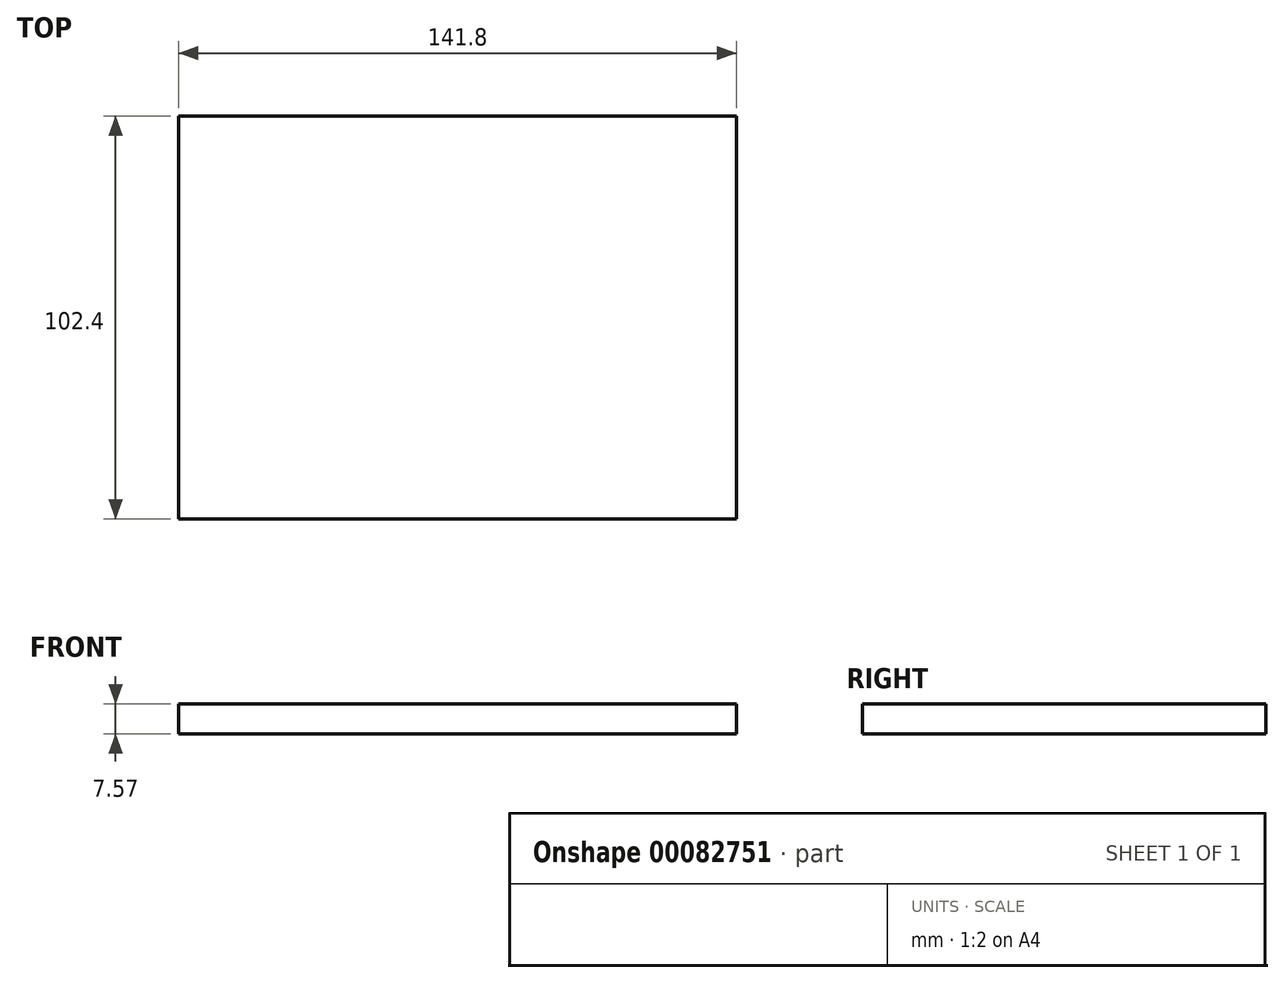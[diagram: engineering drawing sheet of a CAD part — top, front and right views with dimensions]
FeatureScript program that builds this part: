
annotation { "Feature Type Name" : "Feature", "Feature Type Description" : "" }
export const myFeature = defineFeature(function(context is Context, id is Id, definition is map)
    precondition{}
    {
        {
            var Q0;
            Q0=qCreatedBy(makeId("Top.planeOp"),FACE);
            var sketch = newSketch(context, id + "F0", { "sketchPlane" : qUnion([Q0])});
            skLineSegment(sketch, "E0.bottom", {"start": v(-70.05, 51.74) * mm, "end": v(71.75, 51.74) * mm});
            skLineSegment(sketch, "E0.top", {"start": v(-70.05, -50.66) * mm, "end": v(71.75, -50.66) * mm});
            skLineSegment(sketch, "E0.left", {"start": v(-70.05, 51.74) * mm, "end": v(-70.05, -50.66) * mm});
            skLineSegment(sketch, "E0.right", {"start": v(71.75, 51.74) * mm, "end": v(71.75, -50.66) * mm});
            skSolve(sketch);
        }
        {
            var Q0;
            Q0=makeQuery(id+"F0.imprint","IMPRINT",FACE,{"disambiguationData":[TD([[makeQuery(id+"F0.imprint","IMPRINT",EDGE,{"derivedFrom":sQuery(id+"F0.wireOp",EDGE,"E0.bottom")}),-1.0]])]});
            extrude(context, id + "F1", {"entities" : qUnion([Q0]), "depth" : 7.57 * mm});
        }
    });
